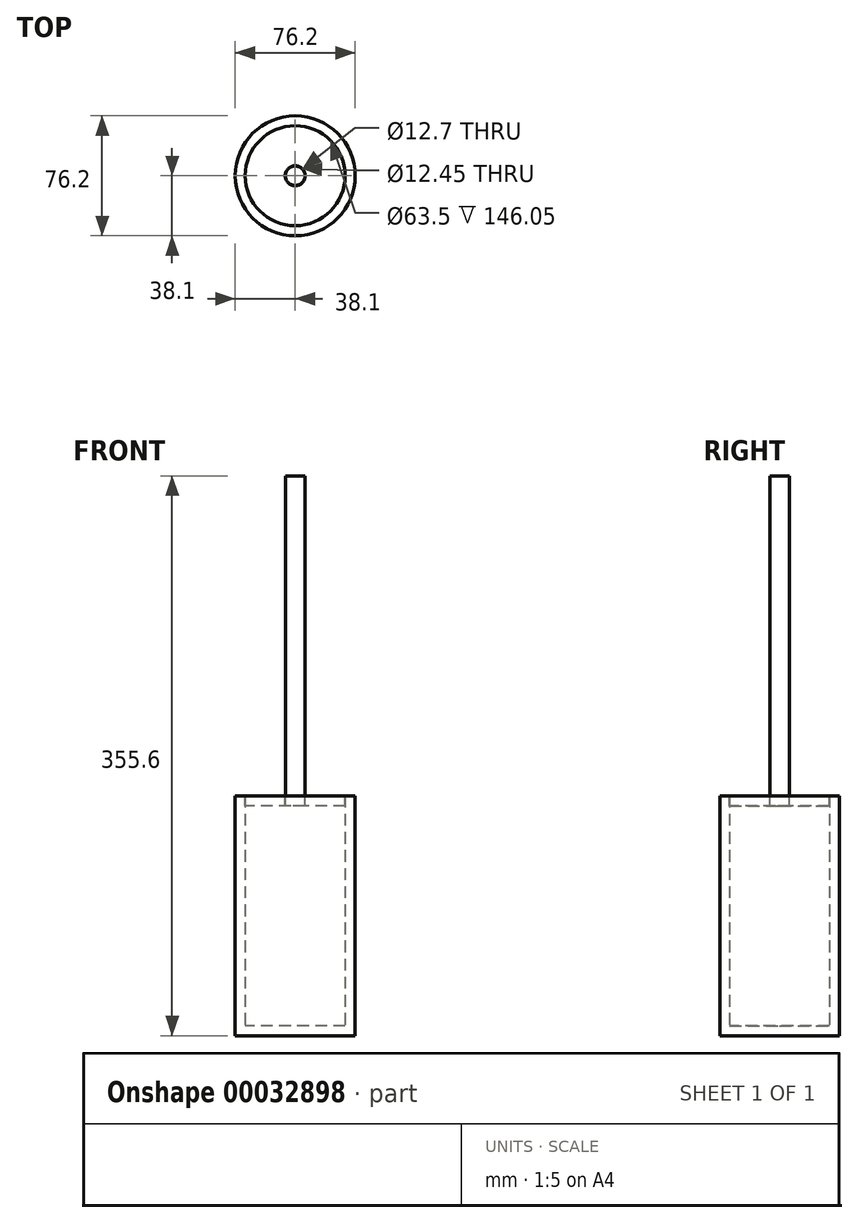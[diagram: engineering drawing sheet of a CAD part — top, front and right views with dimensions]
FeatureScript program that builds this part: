
annotation { "Feature Type Name" : "Feature", "Feature Type Description" : "" }
export const myFeature = defineFeature(function(context is Context, id is Id, definition is map)
    precondition{}
    {
        {
            var Q0;
            Q0=qCreatedBy(makeId("Top.planeOp"),FACE);
            var sketch = newSketch(context, id + "F0", { "sketchPlane" : qUnion([Q0])});
            skCircle(sketch, "E0", {"center": v(0, 0) * mm, "radius": 38.1 * mm});
            skSolve(sketch);
        }
        {
            var Q0;
            Q0 = qSketchRegion(id + "F0", true);
            extrude(context, id + "F1", {"entities" : qUnion([Q0]), "endBound" : BoundingType.SYMMETRIC, "depth" : 152.4 * mm});
        }
        {
            var Q0;
            Q0=makeQuery(id+"F1.opExtrude","CAP_FACE",FACE,{"disambiguationData":[OSD([sQuery(id+"F0.wireOp",EDGE,"E0")])],"isStart":false});
            shell(context, id + "F2", {"entities" : qUnion([Q0]), "thickness" : 6.35 * mm});
        }
        {
            var Q0;
            Q0=makeQuery(id+"F1.opExtrude","CAP_FACE",FACE,{"disambiguationData":[OSD([sQuery(id+"F0.wireOp",EDGE,"E0")])],"isStart":false});
            var sketch = newSketch(context, id + "F3", { "sketchPlane" : qUnion([Q0])});
            skCircle(sketch, "E1.0", {"center": v(0, 0) * mm, "radius": 31.75 * mm});
            skSolve(sketch);
        }
        {
            var Q0;
            Q0=makeQuery(id+"F3.imprint","IMPRINT",FACE,{"disambiguationData":[TD([[makeQuery(id+"F3.imprint","IMPRINT",EDGE,{"derivedFrom":sQuery(id+"F3.wireOp",EDGE,"E1.0")}),1.0]])]});
            extrude(context, id + "F4", {"entities" : qUnion([Q0]), "oppositeDirection" : true, "depth" : 6.35 * mm});
        }
        {
            var Q0;
            Q0=sQuery(id+"F3.wireOp",VERTEX,"E1.0.center");
            var Q1;
            Q1=makeQuery(id+"F4.opExtrude","SWEPT_BODY",BODY,{"disambiguationData":[OSD([sQuery(id+"F3.wireOp",EDGE,"E1.0")])]});
            hole(context, id + "F5", {"style" : HoleStyle.SIMPLE, "holeDiameter" : 12.7 * mm, "endStyle" : HoleEndStyle.THROUGH, "locations" : qUnion([Q0]), "scope" : qUnion([Q1])});
        }
        {
            var Q0;
            Q0=makeQuery(id+"F3.imprint","IMPRINT",FACE,{"disambiguationData":[TD([[makeQuery(id+"F3.imprint","IMPRINT",EDGE,{"derivedFrom":sQuery(id+"F3.wireOp",EDGE,"E1.0")}),1.0]])]});
            var sketch = newSketch(context, id + "F6", { "sketchPlane" : qUnion([Q0])});
            skCircle(sketch, "E2", {"center": v(0, 0) * mm, "radius": 6.22 * mm});
            skSolve(sketch);
        }
        {
            var Q0;
            Q0=makeQuery(id+"F6.imprint","IMPRINT",FACE,{"disambiguationData":[TD([[makeQuery(id+"F6.imprint","IMPRINT",EDGE,{"derivedFrom":sQuery(id+"F6.wireOp",EDGE,"E2")}),1.0]])]});
            extrude(context, id + "F7", {"entities" : qUnion([Q0]), "depth" : 203.2 * mm});
        }
        {
            var Q0;
            Q0=makeQuery(id+"F7.opExtrude","CAP_FACE",FACE,{"disambiguationData":[OSD([sQuery(id+"F6.wireOp",EDGE,"E2")])],"isStart":true});
            var sketch = newSketch(context, id + "F8", { "sketchPlane" : qUnion([Q0])});
            skCircle(sketch, "E3.0", {"center": v(0, 0) * mm, "radius": 6.22 * mm});
            skCircle(sketch, "E4", {"center": v(0, 0) * mm, "radius": 31.75 * mm});
            skSolve(sketch);
        }
        {
            var Q0;
            Q0=makeQuery(id+"F8.imprint","IMPRINT",FACE,{"disambiguationData":[TD([[makeQuery(id+"F8.imprint","IMPRINT",EDGE,{"derivedFrom":sQuery(id+"F8.wireOp",EDGE,"E3.0")}),1.0]])]});
            extrude(context, id + "F9", {"entities" : qUnion([Q0]), "depth" : 6.35 * mm});
        }
    });
